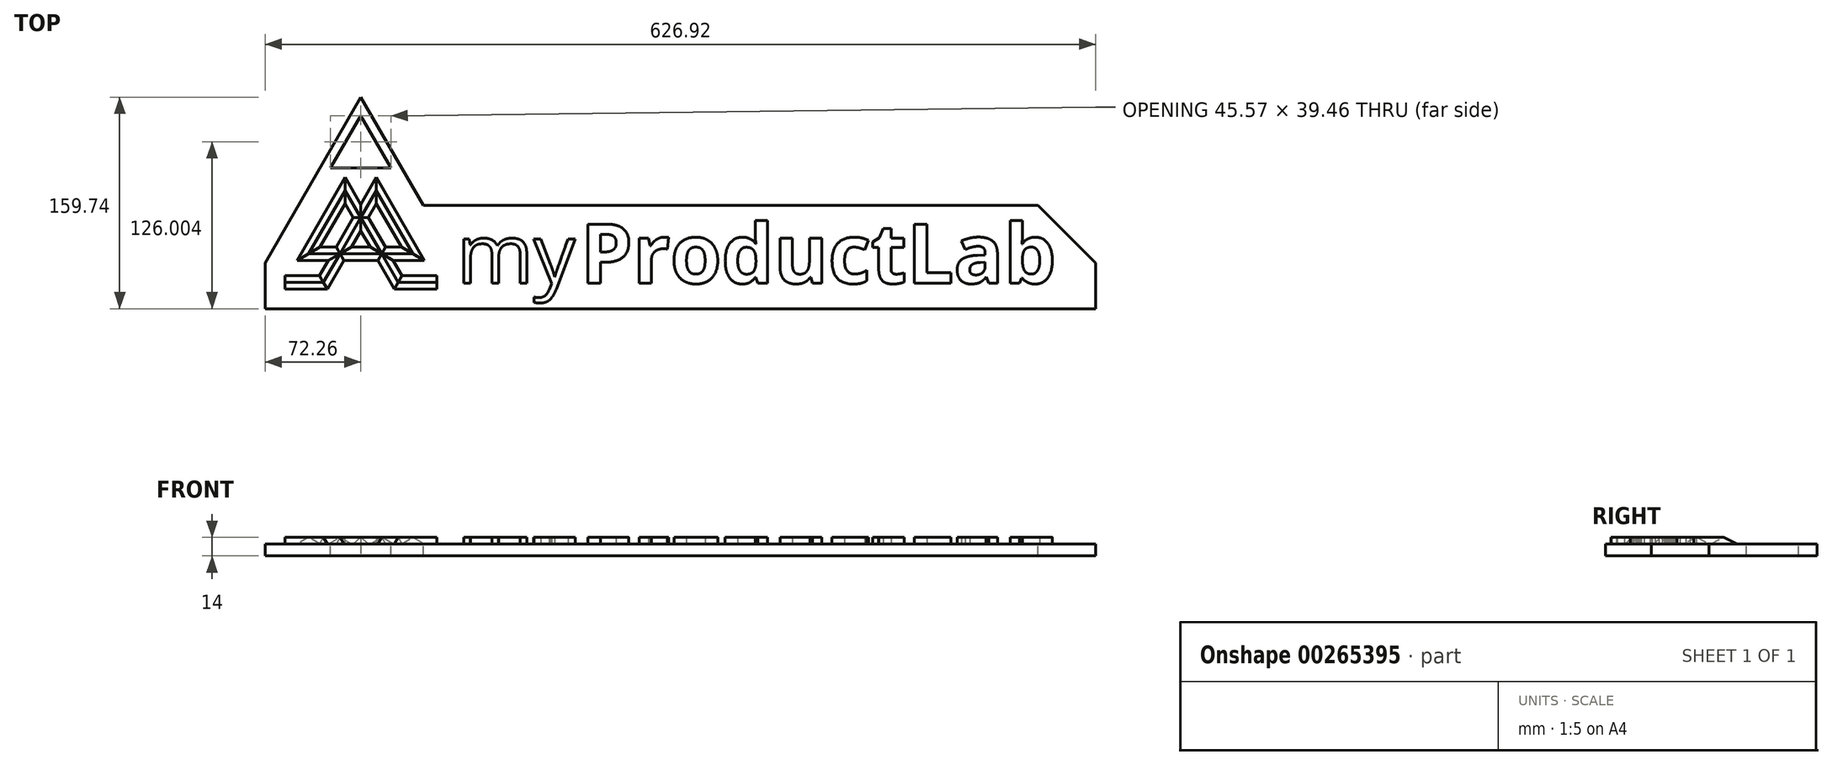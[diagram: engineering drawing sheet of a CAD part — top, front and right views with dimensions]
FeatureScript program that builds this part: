
annotation { "Feature Type Name" : "Feature", "Feature Type Description" : "" }
export const myFeature = defineFeature(function(context is Context, id is Id, definition is map)
    precondition{}
    {
        {
            var Q0;
            Q0=qCreatedBy(makeId("Top.planeOp"),FACE);
            var sketch = newSketch(context, id + "F0", { "sketchPlane" : qUnion([Q0])});
            skLineSegment(sketch, "E0", {"start": v(11.81, 20.46) * mm, "end": v(39.36, -27.25) * mm});
            skLineSegment(sketch, "E1", {"start": v(-39.36, -27.25) * mm, "end": v(-11.81, 20.46) * mm});
            skLineSegment(sketch, "E2", {"start": v(-11.81, 20.46) * mm, "end": v(28.18, -48.8) * mm});
            skLineSegment(sketch, "E3", {"start": v(28.18, -48.8) * mm, "end": v(57.26, -48.8) * mm});
            skLineSegment(sketch, "E4", {"start": v(-28.18, -48.8) * mm, "end": v(-57.26, -48.8) * mm});
            skLineSegment(sketch, "E5", {"start": v(-28.18, -48.8) * mm, "end": v(11.81, 20.46) * mm});
            skLineSegment(sketch, "E6", {"start": v(-39.36, -27.25) * mm, "end": v(0, -27.25) * mm});
            skLineSegment(sketch, "E7", {"start": v(0, -27.25) * mm, "end": v(39.36, -27.25) * mm});
            skSolve(sketch);
        }
        {
            var Q0;
            Q0=sQuery(id+"F0.wireOp",VERTEX,"E4.end");
            var Q1;
            Q1=sQuery(id+"F0.wireOp",EDGE,"E4");
            cPlane(context, id + "F1", {"entities" : qUnion([Q0, Q1]), "cplaneType" : CPlaneType.LINE_POINT, "offset" : 25 * mm, "width" : 150 * mm, "height" : 150 * mm});
        }
        {
            var Q0;
            Q0=qCreatedBy(id+"F1.planeOp",FACE);
            var sketch = newSketch(context, id + "F2", { "sketchPlane" : qUnion([Q0])});
            skLineSegment(sketch, "E8", {"start": v(48.8, 0) * mm, "end": v(43.8, -5) * mm});
            skLineSegment(sketch, "E9", {"start": v(43.8, -5) * mm, "end": v(53.8, -5) * mm});
            skLineSegment(sketch, "E10", {"start": v(53.8, -5) * mm, "end": v(48.8, 0) * mm});
            skSolve(sketch);
        }
        {
            var Q0;
            Q0=qSketchRegion(id+"F2",true);
            var Q1;
            Q1=sQuery(id+"F0.wireOp",EDGE,"E4");
            var Q2;
            Q2=sQuery(id+"F0.wireOp",EDGE,"E5");
            var Q3;
            Q3=sQuery(id+"F0.wireOp",EDGE,"E0");
            var Q4;
            Q4=sQuery(id+"F0.wireOp",EDGE,"E7");
            sweep(context, id + "F3", {"profiles" : qUnion([Q0]), "path" : qUnion([Q1, Q2, Q3, Q4])});
        }
        {
            var Q0;
            Q0=makeQuery(id+"F3.opSweep","SWEPT_BODY",BODY,{"disambiguationData":[OSD([sQuery(id+"F0.wireOp",EDGE,"E7"),sQuery(id+"F2.wireOp",EDGE,"E8"),sQuery(id+"F2.wireOp",EDGE,"E9"),sQuery(id+"F2.wireOp",EDGE,"E10")])]});
            var Q1;
            Q1=qCreatedBy(makeId("Right.planeOp"),FACE);
            mirror(context, id + "F4", {"operationType" : NewBodyOperationType.ADD, "entities" : qUnion([Q0]), "mirrorPlane" : qUnion([Q1])});
        }
        {
            var Q0;
            {var subQ0=makeQuery(id+"F3.opSweep","SWEPT_FACE",FACE,{"disambiguationData":[OSD([sQuery(id+"F0.wireOp",EDGE,"E4"),sQuery(id+"F2.wireOp",EDGE,"E9")])]});Q0=makeQuery(id+"F4.boolean.opBoolean","MERGE",FACE,{"derivedFrom":[subQ0,makeQuery(id+"F4.opPattern","COPY",FACE,{"derivedFrom":subQ0,"instanceName":"1"})]});}
            var sketch = newSketch(context, id + "F5", { "sketchPlane" : qUnion([Q0])});
            skLineSegment(sketch, "E11", {"start": v(-72.26, 68.8) * mm, "end": v(-72.26, -45.46) * mm});
            skLineSegment(sketch, "E12", {"start": v(-72.26, -45.46) * mm, "end": v(-8.93, -45.46) * mm});
            skLineSegment(sketch, "E13", {"start": v(8.93, -45.46) * mm, "end": v(557.26, -45.46) * mm});
            skLineSegment(sketch, "E14", {"start": v(557.26, 68.8) * mm, "end": v(-72.26, 68.8) * mm});
            skLineSegment(sketch, "E15", {"start": v(-32.02, -35.46) * mm, "end": v(-62.26, -35.46) * mm});
            skLineSegment(sketch, "E16", {"start": v(-62.26, -35.46) * mm, "end": v(-62.26, 16.92) * mm});
            skLineSegment(sketch, "E17", {"start": v(-62.26, 16.92) * mm, "end": v(-32.02, -35.46) * mm});
            skPoint(sketch, "E18.orphan", {"position": v(597.26, -45.46) * mm});
            skLineSegment(sketch, "E19", {"start": v(557.26, -45.46) * mm, "end": v(557.26, 68.8) * mm});
            skPoint(sketch, "E20.start.orphan", {"position": v(597.26, -15.46) * mm});
            skPoint(sketch, "E21.end.orphan", {"position": v(597.26, 38.8) * mm});
            skLineSegment(sketch, "E22", {"start": v(-8.93, -45.46) * mm, "end": v(8.93, -45.46) * mm});
            skPoint(sketch, "E23.end.orphan", {"position": v(0, -35) * mm});
            skSolve(sketch);
        }
        {
            var Q0;
            Q0 = qSketchRegion(id + "F5", true);
            extrude(context, id + "F6", {"entities" : qUnion([Q0]), "operationType" : NewBodyOperationType.ADD, "depth" : 5 * mm});
        }
        {
            var Q0;
            {var subQ0=sQuery(id+"F5.wireOp",EDGE,"E14");var subQ1=sQuery(id+"F5.wireOp",EDGE,"E13");var subQ2=sQuery(id+"F5.wireOp",EDGE,"E11");var subQ3=sQuery(id+"F5.wireOp",EDGE,"E23");var subQ4=sQuery(id+"F5.wireOp",EDGE,"E12");var subQ5=sQuery(id+"F5.wireOp",EDGE,"E20");var subQ6=sQuery(id+"F2.wireOp",EDGE,"E8");var subQ7=makeQuery(id+"F3.opSweep","SWEPT_FACE",FACE,{"disambiguationData":[OSD([sQuery(id+"F0.wireOp",EDGE,"E7"),subQ6])]});var subQ8=sQuery(id+"F5.wireOp",EDGE,"E15");var subQ9=sQuery(id+"F2.wireOp",EDGE,"E10");var subQ10=sQuery(id+"F0.wireOp",EDGE,"E4");var subQ11=makeQuery(id+"F3.opSweep","SWEPT_FACE",FACE,{"disambiguationData":[OSD([subQ10,subQ9])]});var subQ12=sQuery(id+"F0.wireOp",EDGE,"E5");var subQ13=makeQuery(id+"F3.opSweep","SWEPT_FACE",FACE,{"disambiguationData":[OSD([subQ12,subQ9])]});var subQ14=makeQuery(id+"F3.opSweep","SWEPT_FACE",FACE,{"disambiguationData":[OSD([subQ10,subQ6])]});var subQ15=makeQuery(id+"F3.opSweep","SWEPT_FACE",FACE,{"disambiguationData":[OSD([sQuery(id+"F0.wireOp",EDGE,"E0"),subQ6])]});var subQ16=makeQuery(id+"F3.opSweep","CAP_FACE",FACE,{"disambiguationData":[OSD([sQuery(id+"F0.wireOp",VERTEX,"E4.end"),subQ6,sQuery(id+"F2.wireOp",EDGE,"E9"),subQ9])],"isStart":true});var subQ17=makeQuery(id+"F3.opSweep","SWEPT_FACE",FACE,{"disambiguationData":[OSD([subQ12,subQ6])]});var subQ18=sQuery(id+"F5.wireOp",EDGE,"J89TbGMw-nEVW-EWQc-egT6-3zY5aMVhYpZx");var subQ19=sQuery(id+"F5.wireOp",EDGE,"E16");var subQ20=sQuery(id+"F5.wireOp",EDGE,"E17");Q0=makeQuery(id+"F6.boolean.opBoolean","SPLIT",FACE,{"disambiguationData":[TD([subQ16,subQ15,subQ14,subQ11,subQ17,subQ13,subQ7,makeQuery(id+"F4.opPattern","COPY",FACE,{"derivedFrom":subQ16,"instanceName":"1"}),makeQuery(id+"F4.opPattern","COPY",FACE,{"derivedFrom":subQ15,"instanceName":"1"}),makeQuery(id+"F4.opPattern","COPY",FACE,{"derivedFrom":subQ14,"instanceName":"1"}),makeQuery(id+"F4.opPattern","COPY",FACE,{"derivedFrom":subQ11,"instanceName":"1"}),makeQuery(id+"F4.opPattern","COPY",FACE,{"derivedFrom":subQ17,"instanceName":"1"}),makeQuery(id+"F4.opPattern","COPY",FACE,{"derivedFrom":subQ13,"instanceName":"1"}),makeQuery(id+"F4.opPattern","COPY",FACE,{"derivedFrom":subQ7,"instanceName":"1"}),makeQuery(id+"F6.opExtrude","SWEPT_FACE",FACE,{"disambiguationData":[OSD([subQ2])]}),makeQuery(id+"F6.opExtrude","SWEPT_FACE",FACE,{"disambiguationData":[OSD([subQ4])]}),makeQuery(id+"F6.opExtrude","SWEPT_FACE",FACE,{"disambiguationData":[OSD([subQ3])]}),makeQuery(id+"F6.opExtrude","SWEPT_FACE",FACE,{"disambiguationData":[OSD([subQ18])]}),makeQuery(id+"F6.opExtrude","SWEPT_FACE",FACE,{"disambiguationData":[OSD([subQ1])]}),makeQuery(id+"F6.opExtrude","SWEPT_FACE",FACE,{"disambiguationData":[OSD([subQ5])]}),makeQuery(id+"F6.opExtrude","SWEPT_FACE",FACE,{"disambiguationData":[OSD([subQ0])]}),makeQuery(id+"F6.opExtrude","SWEPT_FACE",FACE,{"disambiguationData":[OSD([subQ8])]}),makeQuery(id+"F6.opExtrude","SWEPT_FACE",FACE,{"disambiguationData":[OSD([subQ19])]}),makeQuery(id+"F6.opExtrude","SWEPT_FACE",FACE,{"disambiguationData":[OSD([subQ20])]})])],"derivedFrom":makeQuery(id+"F6.opExtrude","CAP_FACE",FACE,{"disambiguationData":[OSD([subQ2,subQ4,subQ3,subQ18,subQ1,subQ5,subQ0,subQ8,subQ19,subQ20])],"isStart":true})});}
            var sketch = newSketch(context, id + "F7", { "sketchPlane" : qUnion([Q0])});
            skText(sketch, "E24", { "text": "my", "fontName": "OpenSans-Regular.ttf"});
            skText(sketch, "E25", { "text": "ProductLab", "fontName": "OpenSans-Bold.ttf"});
            const initialGuessF7  = {"E24": [0.07226, -0.04954, 1, 0, 0.045], "E25": [0.16589, -0.04954, 1, 0, 0.045]};
            skSetInitialGuess(sketch, initialGuessF7);
            skSolve(sketch);
        }
        {
            var Q0;
            Q0 = qSketchRegion(id + "F7", true);
            extrude(context, id + "F8", {"entities" : qUnion([Q0]), "operationType" : NewBodyOperationType.ADD, "depth" : 5 * mm});
        }
        {
            var Q0;
            {var subQ0=sQuery(id+"F5.wireOp",EDGE,"J89TbGMw-nEVW-EWQc-egT6-3zY5aMVhYpZx");var subQ1=makeQuery(id+"F6.opExtrude","SWEPT_FACE",FACE,{"disambiguationData":[OSD([subQ0])]});var subQ2=sQuery(id+"F5.wireOp",EDGE,"E20");var subQ3=makeQuery(id+"F6.opExtrude","SWEPT_FACE",FACE,{"disambiguationData":[OSD([subQ2])]});var subQ4=sQuery(id+"F5.wireOp",EDGE,"Xyr0NvYb-IOld-dSm6-9Bcy-tAYvncZcYHa3");var subQ5=makeQuery(id+"F6.opExtrude","SWEPT_FACE",FACE,{"disambiguationData":[OSD([subQ4])]});var subQ6=sQuery(id+"F2.wireOp",EDGE,"E8");var subQ7=makeQuery(id+"F3.opSweep","SWEPT_FACE",FACE,{"disambiguationData":[OSD([sQuery(id+"F0.wireOp",EDGE,"E7"),subQ6])]});var subQ8=makeQuery(id+"F4.opPattern","COPY",FACE,{"derivedFrom":subQ7,"instanceName":"1"});var subQ9=sQuery(id+"F0.wireOp",EDGE,"E4");var subQ10=makeQuery(id+"F3.opSweep","SWEPT_FACE",FACE,{"disambiguationData":[OSD([subQ9,subQ6])]});var subQ11=sQuery(id+"F5.wireOp",EDGE,"E21");var subQ12=makeQuery(id+"F6.opExtrude","SWEPT_FACE",FACE,{"disambiguationData":[OSD([subQ11])]});var subQ13=makeQuery(id+"F3.opSweep","SWEPT_FACE",FACE,{"disambiguationData":[OSD([sQuery(id+"F0.wireOp",EDGE,"E0"),subQ6])]});var subQ14=makeQuery(id+"F4.opPattern","COPY",FACE,{"derivedFrom":subQ13,"instanceName":"1"});var subQ15=makeQuery(id+"F4.opPattern","COPY",FACE,{"derivedFrom":subQ10,"instanceName":"1"});var subQ16=sQuery(id+"F5.wireOp",EDGE,"E15");var subQ17=makeQuery(id+"F6.opExtrude","SWEPT_FACE",FACE,{"disambiguationData":[OSD([subQ16])]});var subQ18=sQuery(id+"F0.wireOp",EDGE,"E5");var subQ19=makeQuery(id+"F3.opSweep","SWEPT_FACE",FACE,{"disambiguationData":[OSD([subQ18,subQ6])]});var subQ20=makeQuery(id+"F4.opPattern","COPY",FACE,{"derivedFrom":subQ19,"instanceName":"1"});var subQ21=sQuery(id+"F2.wireOp",EDGE,"E10");var subQ22=makeQuery(id+"F3.opSweep","CAP_FACE",FACE,{"disambiguationData":[OSD([sQuery(id+"F0.wireOp",VERTEX,"E4.end"),subQ6,sQuery(id+"F2.wireOp",EDGE,"E9"),subQ21])],"isStart":true});var subQ23=makeQuery(id+"F3.opSweep","SWEPT_FACE",FACE,{"disambiguationData":[OSD([subQ18,subQ21])]});var subQ24=makeQuery(id+"F3.opSweep","SWEPT_FACE",FACE,{"disambiguationData":[OSD([subQ9,subQ21])]});var subQ25=sQuery(id+"F5.wireOp",EDGE,"E17");var subQ26=makeQuery(id+"F6.opExtrude","SWEPT_FACE",FACE,{"disambiguationData":[OSD([subQ25])]});var subQ27=makeQuery(id+"F4.opPattern","COPY",FACE,{"derivedFrom":subQ23,"instanceName":"1"});var subQ28=sQuery(id+"F5.wireOp",EDGE,"E13");var subQ29=makeQuery(id+"F6.opExtrude","SWEPT_FACE",FACE,{"disambiguationData":[OSD([subQ28])]});var subQ30=makeQuery(id+"F4.opPattern","COPY",FACE,{"derivedFrom":subQ24,"instanceName":"1"});var subQ31=sQuery(id+"F5.wireOp",EDGE,"E11");var subQ32=makeQuery(id+"F6.opExtrude","SWEPT_FACE",FACE,{"disambiguationData":[OSD([subQ31])]});var subQ33=sQuery(id+"F5.wireOp",EDGE,"E23");var subQ34=makeQuery(id+"F6.opExtrude","SWEPT_FACE",FACE,{"disambiguationData":[OSD([subQ33])]});var subQ35=makeQuery(id+"F4.opPattern","COPY",FACE,{"derivedFrom":subQ22,"instanceName":"1"});var subQ36=sQuery(id+"F5.wireOp",EDGE,"E12");var subQ37=makeQuery(id+"F6.opExtrude","SWEPT_FACE",FACE,{"disambiguationData":[OSD([subQ36])]});var subQ38=sQuery(id+"F5.wireOp",EDGE,"E14");var subQ39=makeQuery(id+"F6.opExtrude","SWEPT_FACE",FACE,{"disambiguationData":[OSD([subQ38])]});var subQ40=sQuery(id+"F5.wireOp",EDGE,"E16");var subQ41=makeQuery(id+"F6.opExtrude","SWEPT_FACE",FACE,{"disambiguationData":[OSD([subQ40])]});Q0=makeQuery(id+"F8.boolean.opBoolean","SPLIT",FACE,{"disambiguationData":[TD([subQ32])],"derivedFrom":makeQuery(id+"F6.boolean.opBoolean","SPLIT",FACE,{"disambiguationData":[TD([subQ22,subQ13,subQ10,subQ24,subQ19,subQ23,subQ7,subQ35,subQ14,subQ15,subQ30,subQ20,subQ27,subQ8,subQ32,subQ37,subQ34,subQ1,subQ29,subQ3,subQ39,subQ17,subQ41,subQ26,subQ5,subQ12])],"derivedFrom":makeQuery(id+"F6.opExtrude","CAP_FACE",FACE,{"disambiguationData":[OSD([subQ31,subQ36,subQ33,subQ0,subQ28,subQ2,subQ38,subQ16,subQ40,subQ25,subQ4,subQ11])],"isStart":true})})});}
            var sketch = newSketch(context, id + "F9", { "sketchPlane" : qUnion([Q0])});
            skPoint(sketch, "E26.endSnap0", {"position": v(220.32, -15.58) * mm});
            skLineSegment(sketch, "E27", {"start": v(557.26, -11.67) * mm, "end": v(-293.74, -11.67) * mm, "construction": true});
            skPoint(sketch, "E27.endSnap0", {"position": v(-72.26, -11.67) * mm});
            skLineSegment(sketch, "E28", {"start": v(557.26, 9.24) * mm, "end": v(557.26, 45.46) * mm});
            skLineSegment(sketch, "E29", {"start": v(557.26, 45.46) * mm, "end": v(26.25, 45.46) * mm});
            skLineSegment(sketch, "E30", {"start": v(26.25, 45.46) * mm, "end": v(47.16, 9.24) * mm});
            skLineSegment(sketch, "E31", {"start": v(47.16, 9.24) * mm, "end": v(557.26, 9.24) * mm});
            skSolve(sketch);
        }
        {
            var Q0;
            Q0 = qSketchRegion(id + "F9", true);
            extrude(context, id + "F10", {"entities" : qUnion([Q0]), "operationType" : NewBodyOperationType.REMOVE, "oppositeDirection" : true, "depth" : 25 * mm});
        }
        {
            var Q0;
            Q0=makeQuery(id+"F10.boolean.opBoolean","COPY",EDGE,{"derivedFrom":makeQuery(id+"F10.opExtrude","SWEPT_EDGE",EDGE,{"disambiguationData":[OSD([sQuery(id+"F5.wireOp",EDGE,"E19"),sQuery(id+"F9.wireOp",EDGE,"3NKoLEs0-C7rr-6Oif-dHGT-x0XMBWaBHwz6"),sQuery(id+"F9.wireOp",EDGE,"E28")])]})});
            var Q1;
            Q1=makeQuery(id+"F6.opExtrude","SWEPT_EDGE",EDGE,{"disambiguationData":[OSD([sQuery(id+"F5.wireOp",EDGE,"E14"),sQuery(id+"F5.wireOp",EDGE,"E19")])]});
            chamfer(context, id + "F11", {"entities" : qUnion([Q0, Q1]), "width" : 25 * mm, "tangentPropagation" : true});
        }
        {
            var Q0;
            {var subQ0=sQuery(id+"F5.wireOp",EDGE,"E17");var subQ1=makeQuery(id+"F6.opExtrude","SWEPT_FACE",FACE,{"disambiguationData":[OSD([subQ0])]});var subQ2=sQuery(id+"F5.wireOp",EDGE,"E19");var subQ3=makeQuery(id+"F6.opExtrude","SWEPT_FACE",FACE,{"disambiguationData":[OSD([subQ2])]});var subQ4=sQuery(id+"F5.wireOp",EDGE,"E22");var subQ5=sQuery(id+"F5.wireOp",EDGE,"E13");var subQ6=sQuery(id+"F5.wireOp",EDGE,"E12");var subQ7=makeQuery(id+"F6.opExtrude","SWEPT_FACE",FACE,{"disambiguationData":[OSD([subQ6,subQ5,subQ4])]});var subQ8=sQuery(id+"F2.wireOp",EDGE,"E10");var subQ9=sQuery(id+"F2.wireOp",EDGE,"E8");var subQ10=makeQuery(id+"F3.opSweep","CAP_FACE",FACE,{"disambiguationData":[OSD([sQuery(id+"F0.wireOp",VERTEX,"E4.end"),subQ9,sQuery(id+"F2.wireOp",EDGE,"E9"),subQ8])],"isStart":true});var subQ11=makeQuery(id+"F4.opPattern","COPY",FACE,{"derivedFrom":subQ10,"instanceName":"1"});var subQ12=sQuery(id+"F5.wireOp",EDGE,"E14");var subQ13=makeQuery(id+"F6.opExtrude","SWEPT_FACE",FACE,{"disambiguationData":[OSD([subQ12])]});var subQ14=sQuery(id+"F5.wireOp",EDGE,"E15");var subQ15=makeQuery(id+"F6.opExtrude","SWEPT_FACE",FACE,{"disambiguationData":[OSD([subQ14])]});var subQ16=sQuery(id+"F0.wireOp",EDGE,"E4");var subQ17=makeQuery(id+"F3.opSweep","SWEPT_FACE",FACE,{"disambiguationData":[OSD([subQ16,subQ8])]});var subQ18=makeQuery(id+"F4.opPattern","COPY",FACE,{"derivedFrom":subQ17,"instanceName":"1"});var subQ19=sQuery(id+"F5.wireOp",EDGE,"E16");var subQ20=makeQuery(id+"F6.opExtrude","SWEPT_FACE",FACE,{"disambiguationData":[OSD([subQ19])]});var subQ21=sQuery(id+"F0.wireOp",EDGE,"E5");var subQ22=makeQuery(id+"F3.opSweep","SWEPT_FACE",FACE,{"disambiguationData":[OSD([subQ21,subQ8])]});var subQ23=makeQuery(id+"F4.opPattern","COPY",FACE,{"derivedFrom":subQ22,"instanceName":"1"});var subQ24=makeQuery(id+"F3.opSweep","SWEPT_FACE",FACE,{"disambiguationData":[OSD([subQ16,subQ9])]});var subQ25=makeQuery(id+"F3.opSweep","SWEPT_FACE",FACE,{"disambiguationData":[OSD([sQuery(id+"F0.wireOp",EDGE,"E0"),subQ9])]});var subQ26=makeQuery(id+"F3.opSweep","SWEPT_FACE",FACE,{"disambiguationData":[OSD([subQ21,subQ9])]});var subQ27=makeQuery(id+"F4.opPattern","COPY",FACE,{"derivedFrom":subQ26,"instanceName":"1"});var subQ28=makeQuery(id+"F3.opSweep","SWEPT_FACE",FACE,{"disambiguationData":[OSD([sQuery(id+"F0.wireOp",EDGE,"E7"),subQ9])]});var subQ29=makeQuery(id+"F4.opPattern","COPY",FACE,{"derivedFrom":subQ24,"instanceName":"1"});var subQ30=makeQuery(id+"F4.opPattern","COPY",FACE,{"derivedFrom":subQ25,"instanceName":"1"});var subQ31=makeQuery(id+"F4.opPattern","COPY",FACE,{"derivedFrom":subQ28,"instanceName":"1"});var subQ32=sQuery(id+"F5.wireOp",EDGE,"E11");var subQ33=makeQuery(id+"F6.opExtrude","SWEPT_FACE",FACE,{"disambiguationData":[OSD([subQ32])]});Q0=makeQuery(id+"F8.boolean.opBoolean","SPLIT",FACE,{"disambiguationData":[TD([subQ33])],"derivedFrom":makeQuery(id+"F6.boolean.opBoolean","SPLIT",FACE,{"disambiguationData":[TD([subQ10,subQ25,subQ24,subQ17,subQ26,subQ22,subQ28,subQ11,subQ30,subQ29,subQ18,subQ27,subQ23,subQ31,subQ33,subQ7,subQ13,subQ15,subQ20,subQ1,subQ3])],"derivedFrom":makeQuery(id+"F6.opExtrude","CAP_FACE",FACE,{"disambiguationData":[OSD([subQ32,subQ6,subQ5,subQ12,subQ14,subQ19,subQ0,subQ2,subQ4])],"isStart":true})})});}
            var sketch = newSketch(context, id + "F12", { "sketchPlane" : qUnion([Q0])});
            skLineSegment(sketch, "E32.0", {"start": v(-72.26, 45.46) * mm, "end": v(26.25, 45.46) * mm});
            skPoint(sketch, "E33.0", {"position": v(36.7, 27.35) * mm});
            skLineSegment(sketch, "E34.0", {"start": v(26.25, 45.46) * mm, "end": v(47.16, 9.24) * mm});
            skLineSegment(sketch, "E35.0", {"start": v(47.16, 9.24) * mm, "end": v(532.26, 9.24) * mm});
            skPoint(sketch, "E36.0", {"position": v(544.76, -3.26) * mm});
            skPoint(sketch, "E37.0", {"position": v(557.26, -29.78) * mm});
            skLineSegment(sketch, "E38.0", {"start": v(557.26, -15.76) * mm, "end": v(557.26, -43.8) * mm});
            skLineSegment(sketch, "E39.0", {"start": v(557.26, -15.76) * mm, "end": v(532.26, 9.24) * mm});
            skLineSegment(sketch, "E40.0", {"start": v(532.26, -68.8) * mm, "end": v(557.26, -43.8) * mm});
            skLineSegment(sketch, "E41.0", {"start": v(532.26, -68.8) * mm, "end": v(-72.26, -68.8) * mm});
            skLineSegment(sketch, "E42.0", {"start": v(-72.26, -68.8) * mm, "end": v(-72.26, 45.46) * mm});
            skLineSegment(sketch, "E43.0", {"start": v(22.78, 39.46) * mm, "end": v(43.7, 3.24) * mm});
            skLineSegment(sketch, "E43.1", {"start": v(-66.26, 39.46) * mm, "end": v(22.78, 39.46) * mm});
            skLineSegment(sketch, "E43.2", {"start": v(43.7, 3.24) * mm, "end": v(529.78, 3.24) * mm});
            skLineSegment(sketch, "E43.3", {"start": v(-66.26, -62.8) * mm, "end": v(-66.26, 39.46) * mm});
            skLineSegment(sketch, "E43.4", {"start": v(551.26, -18.25) * mm, "end": v(529.78, 3.24) * mm});
            skLineSegment(sketch, "E43.5", {"start": v(551.26, -18.25) * mm, "end": v(551.26, -41.32) * mm});
            skLineSegment(sketch, "E43.6", {"start": v(529.78, -62.8) * mm, "end": v(551.26, -41.32) * mm});
            skLineSegment(sketch, "E43.7", {"start": v(529.78, -62.8) * mm, "end": v(-66.26, -62.8) * mm});
            skSolve(sketch);
        }
        {
            var Q0;
            Q0=makeQuery(id+"F12.imprint","IMPRINT",FACE,{"disambiguationData":[TD([[makeQuery(id+"F12.imprint","IMPRINT",EDGE,{"derivedFrom":sQuery(id+"F12.wireOp",EDGE,"E43.0")}),-1.0]])]});
            var sketch = newSketch(context, id + "F13", { "sketchPlane" : qUnion([Q0])});
            skLineSegment(sketch, "E44", {"start": v(26.25, 45.46) * mm, "end": v(532.26, 9.24) * mm});
            skLineSegment(sketch, "E45", {"start": v(532.26, 9.24) * mm, "end": v(462.24, 9.24) * mm});
            skLineSegment(sketch, "E46", {"start": v(462.24, 9.24) * mm, "end": v(29.27, 40.23) * mm});
            skLineSegment(sketch, "E47", {"start": v(29.27, 40.23) * mm, "end": v(26.25, 45.46) * mm});
            skSolve(sketch);
        }
        {
            var Q0;
            Q0 = qSketchRegion(id + "F13", true);
            extrude(context, id + "F14", {"entities" : qUnion([Q0]), "operationType" : NewBodyOperationType.ADD, "oppositeDirection" : true, "depth" : 5 * mm});
        }
        {
            var Q0;
            Q0=makeQuery(id+"F12.imprint","IMPRINT",FACE,{"disambiguationData":[TD([[makeQuery(id+"F12.imprint","IMPRINT",EDGE,{"derivedFrom":sQuery(id+"F12.wireOp",EDGE,"E43.0")}),-1.0]])]});
            var sketch = newSketch(context, id + "F15", { "sketchPlane" : qUnion([Q0])});
            skSolve(sketch);
        }
        {
            var Q0;
            Q0=makeQuery(id+"F14.boolean.opBoolean","MERGE",FACE,{"derivedFrom":[makeQuery(id+"F6.opExtrude","CAP_FACE",FACE,{"disambiguationData":[OSD([sQuery(id+"F5.wireOp",EDGE,"E11"),sQuery(id+"F5.wireOp",EDGE,"E12"),sQuery(id+"F5.wireOp",EDGE,"E13"),sQuery(id+"F5.wireOp",EDGE,"E14"),sQuery(id+"F5.wireOp",EDGE,"E15"),sQuery(id+"F5.wireOp",EDGE,"E16"),sQuery(id+"F5.wireOp",EDGE,"E17"),sQuery(id+"F5.wireOp",EDGE,"E19"),sQuery(id+"F5.wireOp",EDGE,"E22")])],"isStart":false}),makeQuery(id+"F14.opExtrude","CAP_FACE",FACE,{"disambiguationData":[OSD([sQuery(id+"F13.wireOp",EDGE,"E44"),sQuery(id+"F13.wireOp",EDGE,"E45"),sQuery(id+"F13.wireOp",EDGE,"E46"),sQuery(id+"F13.wireOp",EDGE,"E47")])],"isStart":false})]});
            var sketch = newSketch(context, id + "F16", { "sketchPlane" : qUnion([Q0])});
            skLineSegment(sketch, "E48", {"start": v(-72.26, -45.46) * mm, "end": v(-72.26, -50.46) * mm});
            skLineSegment(sketch, "E49.0", {"start": v(534.33, 73.8) * mm, "end": v(-72.26, 73.8) * mm});
            skLineSegment(sketch, "E49.1", {"start": v(534.33, 73.8) * mm, "end": v(562.26, 45.88) * mm});
            skLineSegment(sketch, "E49.2", {"start": v(-72.26, -50.46) * mm, "end": v(26.43, -50.46) * mm});
            skLineSegment(sketch, "E49.3", {"start": v(26.43, -50.46) * mm, "end": v(534.48, -14.1) * mm});
            skLineSegment(sketch, "E49.4", {"start": v(562.26, 13.69) * mm, "end": v(534.48, -14.1) * mm});
            skLineSegment(sketch, "E49.5", {"start": v(562.26, 13.69) * mm, "end": v(562.26, 45.88) * mm});
            skLineSegment(sketch, "E50", {"start": v(-72.26, 73.8) * mm, "end": v(-72.26, 68.8) * mm});
            skLineSegment(sketch, "E51.0", {"start": v(-72.26, -45.46) * mm, "end": v(26.25, -45.46) * mm});
            skLineSegment(sketch, "E52.0", {"start": v(26.25, -45.46) * mm, "end": v(532.26, -9.24) * mm});
            skLineSegment(sketch, "E53.0", {"start": v(557.26, 15.76) * mm, "end": v(532.26, -9.24) * mm});
            skLineSegment(sketch, "E54.0", {"start": v(557.26, 15.76) * mm, "end": v(557.26, 43.8) * mm});
            skLineSegment(sketch, "E55.0", {"start": v(532.26, 68.8) * mm, "end": v(557.26, 43.8) * mm});
            skLineSegment(sketch, "E56.0", {"start": v(532.26, 68.8) * mm, "end": v(-72.26, 68.8) * mm});
            skSolve(sketch);
        }
        {
            var Q0;
            Q0 = qSketchRegion(id + "F16", true);
            extrude(context, id + "F17", {"entities" : qUnion([Q0]), "operationType" : NewBodyOperationType.ADD, "oppositeDirection" : true, "depth" : 5 * mm});
        }
        {
            var Q0;
            Q0=makeQuery(id+"F15.imprint","IMPRINT",FACE,{"disambiguationData":[TD([[makeQuery(id+"F15.imprint","IMPRINT",EDGE,{"derivedFrom":makeQuery(id+"F12.imprint","IMPRINT",EDGE,{"derivedFrom":sQuery(id+"F12.wireOp",EDGE,"E43.0")})}),-1.0]])]});
            var sketch = newSketch(context, id + "F18", { "sketchPlane" : qUnion([Q0])});
            skLineSegment(sketch, "E57", {"start": v(-95.15, -73.88) * mm, "end": v(-7.88, 77.28) * mm});
            skLineSegment(sketch, "E58", {"start": v(-7.88, 77.28) * mm, "end": v(-102.86, 77.28) * mm});
            skLineSegment(sketch, "E59", {"start": v(-102.86, 77.28) * mm, "end": v(-95.15, -73.88) * mm});
            skSolve(sketch);
        }
        {
            var Q0;
            Q0 = qSketchRegion(id + "F18", true);
            extrude(context, id + "F19", {"entities" : qUnion([Q0]), "operationType" : NewBodyOperationType.REMOVE, "oppositeDirection" : true, "depth" : 25 * mm});
        }
        {
            var Q0;
            Q0=makeQuery(id+"F15.imprint","IMPRINT",FACE,{"disambiguationData":[TD([[makeQuery(id+"F15.imprint","IMPRINT",EDGE,{"derivedFrom":makeQuery(id+"F12.imprint","IMPRINT",EDGE,{"derivedFrom":sQuery(id+"F12.wireOp",EDGE,"E43.0")})}),-1.0]])]});
            var sketch = newSketch(context, id + "F20", { "sketchPlane" : qUnion([Q0])});
            skLineSegment(sketch, "E60", {"start": v(534.48, 16.87) * mm, "end": v(534.48, -68.8) * mm});
            skLineSegment(sketch, "E61", {"start": v(534.48, -79.9) * mm, "end": v(584.33, -78.57) * mm});
            skLineSegment(sketch, "E62", {"start": v(584.33, -78.57) * mm, "end": v(562.44, 10.18) * mm});
            skLineSegment(sketch, "E63", {"start": v(562.44, 10.18) * mm, "end": v(534.48, 16.87) * mm});
            skLineSegment(sketch, "E64", {"start": v(534.48, -68.8) * mm, "end": v(-141.37, -68.8) * mm});
            skLineSegment(sketch, "E65", {"start": v(-141.37, -68.8) * mm, "end": v(-141.37, -83.35) * mm});
            skLineSegment(sketch, "E66", {"start": v(-141.37, -83.35) * mm, "end": v(534.48, -79.9) * mm});
            skSolve(sketch);
        }
        {
            var Q0;
            Q0 = qSketchRegion(id + "F20", true);
            extrude(context, id + "F21", {"entities" : qUnion([Q0]), "operationType" : NewBodyOperationType.REMOVE, "oppositeDirection" : true, "depth" : 25 * mm});
        }
        {
            var Q0;
            Q0=makeQuery(id+"F17.boolean.opBoolean","MERGE",FACE,{"derivedFrom":[makeQuery(id+"F14.boolean.opBoolean","MERGE",FACE,{"derivedFrom":[makeQuery(id+"F6.opExtrude","CAP_FACE",FACE,{"disambiguationData":[OSD([sQuery(id+"F5.wireOp",EDGE,"E11"),sQuery(id+"F5.wireOp",EDGE,"E12"),sQuery(id+"F5.wireOp",EDGE,"E13"),sQuery(id+"F5.wireOp",EDGE,"E14"),sQuery(id+"F5.wireOp",EDGE,"E15"),sQuery(id+"F5.wireOp",EDGE,"E16"),sQuery(id+"F5.wireOp",EDGE,"E17"),sQuery(id+"F5.wireOp",EDGE,"E19"),sQuery(id+"F5.wireOp",EDGE,"E22")])],"isStart":false}),makeQuery(id+"F14.opExtrude","CAP_FACE",FACE,{"disambiguationData":[OSD([sQuery(id+"F13.wireOp",EDGE,"E44"),sQuery(id+"F13.wireOp",EDGE,"E45"),sQuery(id+"F13.wireOp",EDGE,"E46"),sQuery(id+"F13.wireOp",EDGE,"E47")])],"isStart":false})]}),makeQuery(id+"F17.opExtrude","CAP_FACE",FACE,{"disambiguationData":[OSD([sQuery(id+"F16.wireOp",EDGE,"E48"),sQuery(id+"F16.wireOp",EDGE,"E49.0"),sQuery(id+"F16.wireOp",EDGE,"E49.1"),sQuery(id+"F16.wireOp",EDGE,"E49.2"),sQuery(id+"F16.wireOp",EDGE,"E49.3"),sQuery(id+"F16.wireOp",EDGE,"E49.4"),sQuery(id+"F16.wireOp",EDGE,"E49.5"),sQuery(id+"F16.wireOp",EDGE,"E50"),sQuery(id+"F16.wireOp",EDGE,"E51.0"),sQuery(id+"F16.wireOp",EDGE,"E52.0"),sQuery(id+"F16.wireOp",EDGE,"E53.0"),sQuery(id+"F16.wireOp",EDGE,"E54.0"),sQuery(id+"F16.wireOp",EDGE,"E55.0"),sQuery(id+"F16.wireOp",EDGE,"E56.0")])],"isStart":true})]});
            var sketch = newSketch(context, id + "F22", { "sketchPlane" : qUnion([Q0])});
            skLineSegment(sketch, "E67", {"start": v(534.48, -14.1) * mm, "end": v(534.48, 68.8) * mm});
            skLineSegment(sketch, "E68", {"start": v(534.48, 68.8) * mm, "end": v(581.31, 68.8) * mm});
            skLineSegment(sketch, "E69", {"start": v(581.31, 34.24) * mm, "end": v(534.48, -14.1) * mm});
            skLineSegment(sketch, "E70", {"start": v(581.31, 34.24) * mm, "end": v(581.31, 68.8) * mm});
            skSolve(sketch);
        }
        {
            var Q0;
            Q0 = qSketchRegion(id + "F22", true);
            extrude(context, id + "F23", {"entities" : qUnion([Q0]), "operationType" : NewBodyOperationType.ADD, "oppositeDirection" : true, "depth" : 5 * mm});
        }
        {
            var Q0;
            Q0=makeQuery(id+"F23.boolean.opBoolean","MERGE",FACE,{"derivedFrom":[makeQuery(id+"F17.boolean.opBoolean","MERGE",FACE,{"derivedFrom":[makeQuery(id+"F14.boolean.opBoolean","MERGE",FACE,{"derivedFrom":[makeQuery(id+"F6.opExtrude","CAP_FACE",FACE,{"disambiguationData":[OSD([sQuery(id+"F5.wireOp",EDGE,"E11"),sQuery(id+"F5.wireOp",EDGE,"E12"),sQuery(id+"F5.wireOp",EDGE,"E13"),sQuery(id+"F5.wireOp",EDGE,"E14"),sQuery(id+"F5.wireOp",EDGE,"E15"),sQuery(id+"F5.wireOp",EDGE,"E16"),sQuery(id+"F5.wireOp",EDGE,"E17"),sQuery(id+"F5.wireOp",EDGE,"E19"),sQuery(id+"F5.wireOp",EDGE,"E22")])],"isStart":false}),makeQuery(id+"F14.opExtrude","CAP_FACE",FACE,{"disambiguationData":[OSD([sQuery(id+"F13.wireOp",EDGE,"E44"),sQuery(id+"F13.wireOp",EDGE,"E45"),sQuery(id+"F13.wireOp",EDGE,"E46"),sQuery(id+"F13.wireOp",EDGE,"E47")])],"isStart":false})]}),makeQuery(id+"F17.opExtrude","CAP_FACE",FACE,{"disambiguationData":[OSD([sQuery(id+"F16.wireOp",EDGE,"E48"),sQuery(id+"F16.wireOp",EDGE,"E49.0"),sQuery(id+"F16.wireOp",EDGE,"E49.1"),sQuery(id+"F16.wireOp",EDGE,"E49.2"),sQuery(id+"F16.wireOp",EDGE,"E49.3"),sQuery(id+"F16.wireOp",EDGE,"E49.4"),sQuery(id+"F16.wireOp",EDGE,"E49.5"),sQuery(id+"F16.wireOp",EDGE,"E50"),sQuery(id+"F16.wireOp",EDGE,"E51.0"),sQuery(id+"F16.wireOp",EDGE,"E52.0"),sQuery(id+"F16.wireOp",EDGE,"E53.0"),sQuery(id+"F16.wireOp",EDGE,"E54.0"),sQuery(id+"F16.wireOp",EDGE,"E55.0"),sQuery(id+"F16.wireOp",EDGE,"E56.0")])],"isStart":true})]}),makeQuery(id+"F23.opExtrude","CAP_FACE",FACE,{"disambiguationData":[OSD([sQuery(id+"F22.wireOp",EDGE,"E67"),sQuery(id+"F22.wireOp",EDGE,"E68"),sQuery(id+"F22.wireOp",EDGE,"E69"),sQuery(id+"F22.wireOp",EDGE,"E70")])],"isStart":true})]});
            var sketch = newSketch(context, id + "F24", { "sketchPlane" : qUnion([Q0])});
            skLineSegment(sketch, "E71", {"start": v(47.16, -9.24) * mm, "end": v(23.36, -50.46) * mm});
            skLineSegment(sketch, "E72", {"start": v(23.36, -50.46) * mm, "end": v(544.11, -50.46) * mm});
            skLineSegment(sketch, "E73", {"start": v(544.11, -50.46) * mm, "end": v(539.18, -9.24) * mm});
            skLineSegment(sketch, "E74", {"start": v(539.18, -9.24) * mm, "end": v(47.16, -9.24) * mm});
            skSolve(sketch);
        }
        {
            var Q0;
            Q0 = qSketchRegion(id + "F24", true);
            extrude(context, id + "F25", {"entities" : qUnion([Q0]), "operationType" : NewBodyOperationType.REMOVE, "oppositeDirection" : true, "depth" : 25 * mm});
        }
        {
            var Q0;
            Q0=makeQuery(id+"F23.boolean.opBoolean","MERGE",FACE,{"derivedFrom":[makeQuery(id+"F17.boolean.opBoolean","MERGE",FACE,{"derivedFrom":[makeQuery(id+"F14.boolean.opBoolean","MERGE",FACE,{"derivedFrom":[makeQuery(id+"F6.opExtrude","CAP_FACE",FACE,{"disambiguationData":[OSD([sQuery(id+"F5.wireOp",EDGE,"E11"),sQuery(id+"F5.wireOp",EDGE,"E12"),sQuery(id+"F5.wireOp",EDGE,"E13"),sQuery(id+"F5.wireOp",EDGE,"E14"),sQuery(id+"F5.wireOp",EDGE,"E15"),sQuery(id+"F5.wireOp",EDGE,"E16"),sQuery(id+"F5.wireOp",EDGE,"E17"),sQuery(id+"F5.wireOp",EDGE,"E19"),sQuery(id+"F5.wireOp",EDGE,"E22")])],"isStart":false}),makeQuery(id+"F14.opExtrude","CAP_FACE",FACE,{"disambiguationData":[OSD([sQuery(id+"F13.wireOp",EDGE,"E44"),sQuery(id+"F13.wireOp",EDGE,"E45"),sQuery(id+"F13.wireOp",EDGE,"E46"),sQuery(id+"F13.wireOp",EDGE,"E47")])],"isStart":false})]}),makeQuery(id+"F17.opExtrude","CAP_FACE",FACE,{"disambiguationData":[OSD([sQuery(id+"F16.wireOp",EDGE,"E48"),sQuery(id+"F16.wireOp",EDGE,"E49.0"),sQuery(id+"F16.wireOp",EDGE,"E49.1"),sQuery(id+"F16.wireOp",EDGE,"E49.2"),sQuery(id+"F16.wireOp",EDGE,"E49.3"),sQuery(id+"F16.wireOp",EDGE,"E49.4"),sQuery(id+"F16.wireOp",EDGE,"E49.5"),sQuery(id+"F16.wireOp",EDGE,"E50"),sQuery(id+"F16.wireOp",EDGE,"E51.0"),sQuery(id+"F16.wireOp",EDGE,"E52.0"),sQuery(id+"F16.wireOp",EDGE,"E53.0"),sQuery(id+"F16.wireOp",EDGE,"E54.0"),sQuery(id+"F16.wireOp",EDGE,"E55.0"),sQuery(id+"F16.wireOp",EDGE,"E56.0")])],"isStart":true})]}),makeQuery(id+"F23.opExtrude","CAP_FACE",FACE,{"disambiguationData":[OSD([sQuery(id+"F22.wireOp",EDGE,"E67"),sQuery(id+"F22.wireOp",EDGE,"E68"),sQuery(id+"F22.wireOp",EDGE,"E69"),sQuery(id+"F22.wireOp",EDGE,"E70")])],"isStart":true})]});
            var sketch = newSketch(context, id + "F26", { "sketchPlane" : qUnion([Q0])});
            skLineSegment(sketch, "E75", {"start": v(-23.36, -50.46) * mm, "end": v(0, -90.93) * mm});
            skLineSegment(sketch, "E76", {"start": v(0, -90.93) * mm, "end": v(23.36, -50.46) * mm});
            skLineSegment(sketch, "E77", {"start": v(23.36, -50.46) * mm, "end": v(-23.36, -50.46) * mm});
            skSolve(sketch);
        }
        {
            var Q0;
            Q0 = qSketchRegion(id + "F26", true);
            extrude(context, id + "F27", {"entities" : qUnion([Q0]), "operationType" : NewBodyOperationType.ADD, "oppositeDirection" : true, "depth" : 5 * mm});
        }
        {
            var Q0;
            {var subQ0=sQuery(id+"F5.wireOp",EDGE,"E17");var subQ1=makeQuery(id+"F6.opExtrude","SWEPT_FACE",FACE,{"disambiguationData":[OSD([subQ0])]});var subQ2=sQuery(id+"F5.wireOp",EDGE,"E19");var subQ3=makeQuery(id+"F6.opExtrude","SWEPT_FACE",FACE,{"disambiguationData":[OSD([subQ2])]});var subQ4=sQuery(id+"F5.wireOp",EDGE,"E22");var subQ5=sQuery(id+"F5.wireOp",EDGE,"E13");var subQ6=sQuery(id+"F5.wireOp",EDGE,"E12");var subQ7=makeQuery(id+"F6.opExtrude","SWEPT_FACE",FACE,{"disambiguationData":[OSD([subQ6,subQ5,subQ4])]});var subQ8=sQuery(id+"F2.wireOp",EDGE,"E10");var subQ9=sQuery(id+"F2.wireOp",EDGE,"E8");var subQ10=makeQuery(id+"F3.opSweep","CAP_FACE",FACE,{"disambiguationData":[OSD([sQuery(id+"F0.wireOp",VERTEX,"E4.end"),subQ9,sQuery(id+"F2.wireOp",EDGE,"E9"),subQ8])],"isStart":true});var subQ11=makeQuery(id+"F4.opPattern","COPY",FACE,{"derivedFrom":subQ10,"instanceName":"1"});var subQ12=sQuery(id+"F5.wireOp",EDGE,"E14");var subQ13=makeQuery(id+"F6.opExtrude","SWEPT_FACE",FACE,{"disambiguationData":[OSD([subQ12])]});var subQ14=sQuery(id+"F5.wireOp",EDGE,"E15");var subQ15=makeQuery(id+"F6.opExtrude","SWEPT_FACE",FACE,{"disambiguationData":[OSD([subQ14])]});var subQ16=sQuery(id+"F0.wireOp",EDGE,"E4");var subQ17=makeQuery(id+"F3.opSweep","SWEPT_FACE",FACE,{"disambiguationData":[OSD([subQ16,subQ8])]});var subQ18=makeQuery(id+"F4.opPattern","COPY",FACE,{"derivedFrom":subQ17,"instanceName":"1"});var subQ19=sQuery(id+"F5.wireOp",EDGE,"E16");var subQ20=makeQuery(id+"F6.opExtrude","SWEPT_FACE",FACE,{"disambiguationData":[OSD([subQ19])]});var subQ21=sQuery(id+"F0.wireOp",EDGE,"E5");var subQ22=makeQuery(id+"F3.opSweep","SWEPT_FACE",FACE,{"disambiguationData":[OSD([subQ21,subQ8])]});var subQ23=makeQuery(id+"F4.opPattern","COPY",FACE,{"derivedFrom":subQ22,"instanceName":"1"});var subQ24=makeQuery(id+"F3.opSweep","SWEPT_FACE",FACE,{"disambiguationData":[OSD([subQ16,subQ9])]});var subQ25=makeQuery(id+"F3.opSweep","SWEPT_FACE",FACE,{"disambiguationData":[OSD([sQuery(id+"F0.wireOp",EDGE,"E0"),subQ9])]});var subQ26=makeQuery(id+"F3.opSweep","SWEPT_FACE",FACE,{"disambiguationData":[OSD([subQ21,subQ9])]});var subQ27=makeQuery(id+"F4.opPattern","COPY",FACE,{"derivedFrom":subQ26,"instanceName":"1"});var subQ28=makeQuery(id+"F3.opSweep","SWEPT_FACE",FACE,{"disambiguationData":[OSD([sQuery(id+"F0.wireOp",EDGE,"E7"),subQ9])]});var subQ29=makeQuery(id+"F4.opPattern","COPY",FACE,{"derivedFrom":subQ24,"instanceName":"1"});var subQ30=makeQuery(id+"F4.opPattern","COPY",FACE,{"derivedFrom":subQ25,"instanceName":"1"});var subQ31=makeQuery(id+"F4.opPattern","COPY",FACE,{"derivedFrom":subQ28,"instanceName":"1"});var subQ32=sQuery(id+"F5.wireOp",EDGE,"E11");var subQ33=makeQuery(id+"F6.opExtrude","SWEPT_FACE",FACE,{"disambiguationData":[OSD([subQ32])]});Q0=makeQuery(id+"F27.boolean.opBoolean","MERGE",FACE,{"derivedFrom":[makeQuery(id+"F23.boolean.opBoolean","MERGE",FACE,{"derivedFrom":[makeQuery(id+"F17.boolean.opBoolean","MERGE",FACE,{"derivedFrom":[makeQuery(id+"F14.boolean.opBoolean","MERGE",FACE,{"derivedFrom":[makeQuery(id+"F8.boolean.opBoolean","SPLIT",FACE,{"disambiguationData":[TD([subQ33])],"derivedFrom":makeQuery(id+"F6.boolean.opBoolean","SPLIT",FACE,{"disambiguationData":[TD([subQ10,subQ25,subQ24,subQ17,subQ26,subQ22,subQ28,subQ11,subQ30,subQ29,subQ18,subQ27,subQ23,subQ31,subQ33,subQ7,subQ13,subQ15,subQ20,subQ1,subQ3])],"derivedFrom":makeQuery(id+"F6.opExtrude","CAP_FACE",FACE,{"disambiguationData":[OSD([subQ32,subQ6,subQ5,subQ12,subQ14,subQ19,subQ0,subQ2,subQ4])],"isStart":true})})}),makeQuery(id+"F14.opExtrude","CAP_FACE",FACE,{"disambiguationData":[OSD([sQuery(id+"F13.wireOp",EDGE,"E44"),sQuery(id+"F13.wireOp",EDGE,"E45"),sQuery(id+"F13.wireOp",EDGE,"E46"),sQuery(id+"F13.wireOp",EDGE,"E47")])],"isStart":true})]}),makeQuery(id+"F17.opExtrude","CAP_FACE",FACE,{"disambiguationData":[OSD([sQuery(id+"F16.wireOp",EDGE,"E48"),sQuery(id+"F16.wireOp",EDGE,"E49.0"),sQuery(id+"F16.wireOp",EDGE,"E49.1"),sQuery(id+"F16.wireOp",EDGE,"E49.2"),sQuery(id+"F16.wireOp",EDGE,"E49.3"),sQuery(id+"F16.wireOp",EDGE,"E49.4"),sQuery(id+"F16.wireOp",EDGE,"E49.5"),sQuery(id+"F16.wireOp",EDGE,"E50"),sQuery(id+"F16.wireOp",EDGE,"E51.0"),sQuery(id+"F16.wireOp",EDGE,"E52.0"),sQuery(id+"F16.wireOp",EDGE,"E53.0"),sQuery(id+"F16.wireOp",EDGE,"E54.0"),sQuery(id+"F16.wireOp",EDGE,"E55.0"),sQuery(id+"F16.wireOp",EDGE,"E56.0")])],"isStart":false})]}),makeQuery(id+"F23.opExtrude","CAP_FACE",FACE,{"disambiguationData":[OSD([sQuery(id+"F22.wireOp",EDGE,"E67"),sQuery(id+"F22.wireOp",EDGE,"E68"),sQuery(id+"F22.wireOp",EDGE,"E69"),sQuery(id+"F22.wireOp",EDGE,"E70")])],"isStart":false})]}),makeQuery(id+"F27.opExtrude","CAP_FACE",FACE,{"disambiguationData":[OSD([sQuery(id+"F26.wireOp",EDGE,"E75"),sQuery(id+"F26.wireOp",EDGE,"E76"),sQuery(id+"F26.wireOp",EDGE,"E77")])],"isStart":false})]});}
            var sketch = newSketch(context, id + "F28", { "sketchPlane" : qUnion([Q0])});
            skLineSegment(sketch, "E78.0", {"start": v(0, 76.93) * mm, "end": v(22.78, 37.46) * mm});
            skLineSegment(sketch, "E78.1", {"start": v(-22.78, 37.46) * mm, "end": v(0, 76.93) * mm});
            skLineSegment(sketch, "E79", {"start": v(-22.78, 37.46) * mm, "end": v(22.78, 37.46) * mm});
            skSolve(sketch);
        }
        {
            var Q0;
            Q0 = qSketchRegion(id + "F28", true);
            extrude(context, id + "F29", {"entities" : qUnion([Q0]), "operationType" : NewBodyOperationType.REMOVE, "oppositeDirection" : true, "depth" : 25 * mm});
        }
        {
            var Q0;
            {var subQ0=sQuery(id+"F5.wireOp",EDGE,"E17");var subQ1=makeQuery(id+"F6.opExtrude","SWEPT_FACE",FACE,{"disambiguationData":[OSD([subQ0])]});var subQ2=sQuery(id+"F5.wireOp",EDGE,"E19");var subQ3=makeQuery(id+"F6.opExtrude","SWEPT_FACE",FACE,{"disambiguationData":[OSD([subQ2])]});var subQ4=sQuery(id+"F5.wireOp",EDGE,"E22");var subQ5=sQuery(id+"F5.wireOp",EDGE,"E13");var subQ6=sQuery(id+"F5.wireOp",EDGE,"E12");var subQ7=makeQuery(id+"F6.opExtrude","SWEPT_FACE",FACE,{"disambiguationData":[OSD([subQ6,subQ5,subQ4])]});var subQ8=sQuery(id+"F2.wireOp",EDGE,"E10");var subQ9=sQuery(id+"F2.wireOp",EDGE,"E8");var subQ10=makeQuery(id+"F3.opSweep","CAP_FACE",FACE,{"disambiguationData":[OSD([sQuery(id+"F0.wireOp",VERTEX,"E4.end"),subQ9,sQuery(id+"F2.wireOp",EDGE,"E9"),subQ8])],"isStart":true});var subQ11=makeQuery(id+"F4.opPattern","COPY",FACE,{"derivedFrom":subQ10,"instanceName":"1"});var subQ12=sQuery(id+"F5.wireOp",EDGE,"E14");var subQ13=makeQuery(id+"F6.opExtrude","SWEPT_FACE",FACE,{"disambiguationData":[OSD([subQ12])]});var subQ14=sQuery(id+"F5.wireOp",EDGE,"E15");var subQ15=makeQuery(id+"F6.opExtrude","SWEPT_FACE",FACE,{"disambiguationData":[OSD([subQ14])]});var subQ16=sQuery(id+"F0.wireOp",EDGE,"E4");var subQ17=makeQuery(id+"F3.opSweep","SWEPT_FACE",FACE,{"disambiguationData":[OSD([subQ16,subQ8])]});var subQ18=makeQuery(id+"F4.opPattern","COPY",FACE,{"derivedFrom":subQ17,"instanceName":"1"});var subQ19=sQuery(id+"F5.wireOp",EDGE,"E16");var subQ20=makeQuery(id+"F6.opExtrude","SWEPT_FACE",FACE,{"disambiguationData":[OSD([subQ19])]});var subQ21=sQuery(id+"F0.wireOp",EDGE,"E5");var subQ22=makeQuery(id+"F3.opSweep","SWEPT_FACE",FACE,{"disambiguationData":[OSD([subQ21,subQ8])]});var subQ23=makeQuery(id+"F4.opPattern","COPY",FACE,{"derivedFrom":subQ22,"instanceName":"1"});var subQ24=makeQuery(id+"F3.opSweep","SWEPT_FACE",FACE,{"disambiguationData":[OSD([subQ16,subQ9])]});var subQ25=makeQuery(id+"F3.opSweep","SWEPT_FACE",FACE,{"disambiguationData":[OSD([sQuery(id+"F0.wireOp",EDGE,"E0"),subQ9])]});var subQ26=makeQuery(id+"F3.opSweep","SWEPT_FACE",FACE,{"disambiguationData":[OSD([subQ21,subQ9])]});var subQ27=makeQuery(id+"F4.opPattern","COPY",FACE,{"derivedFrom":subQ26,"instanceName":"1"});var subQ28=makeQuery(id+"F3.opSweep","SWEPT_FACE",FACE,{"disambiguationData":[OSD([sQuery(id+"F0.wireOp",EDGE,"E7"),subQ9])]});var subQ29=makeQuery(id+"F4.opPattern","COPY",FACE,{"derivedFrom":subQ24,"instanceName":"1"});var subQ30=makeQuery(id+"F4.opPattern","COPY",FACE,{"derivedFrom":subQ25,"instanceName":"1"});var subQ31=makeQuery(id+"F4.opPattern","COPY",FACE,{"derivedFrom":subQ28,"instanceName":"1"});var subQ32=sQuery(id+"F5.wireOp",EDGE,"E11");var subQ33=makeQuery(id+"F6.opExtrude","SWEPT_FACE",FACE,{"disambiguationData":[OSD([subQ32])]});Q0=makeQuery(id+"F27.boolean.opBoolean","MERGE",FACE,{"derivedFrom":[makeQuery(id+"F23.boolean.opBoolean","MERGE",FACE,{"derivedFrom":[makeQuery(id+"F17.boolean.opBoolean","MERGE",FACE,{"derivedFrom":[makeQuery(id+"F14.boolean.opBoolean","MERGE",FACE,{"derivedFrom":[makeQuery(id+"F8.boolean.opBoolean","SPLIT",FACE,{"disambiguationData":[TD([subQ33])],"derivedFrom":makeQuery(id+"F6.boolean.opBoolean","SPLIT",FACE,{"disambiguationData":[TD([subQ10,subQ25,subQ24,subQ17,subQ26,subQ22,subQ28,subQ11,subQ30,subQ29,subQ18,subQ27,subQ23,subQ31,subQ33,subQ7,subQ13,subQ15,subQ20,subQ1,subQ3])],"derivedFrom":makeQuery(id+"F6.opExtrude","CAP_FACE",FACE,{"disambiguationData":[OSD([subQ32,subQ6,subQ5,subQ12,subQ14,subQ19,subQ0,subQ2,subQ4])],"isStart":true})})}),makeQuery(id+"F14.opExtrude","CAP_FACE",FACE,{"disambiguationData":[OSD([sQuery(id+"F13.wireOp",EDGE,"E44"),sQuery(id+"F13.wireOp",EDGE,"E45"),sQuery(id+"F13.wireOp",EDGE,"E46"),sQuery(id+"F13.wireOp",EDGE,"E47")])],"isStart":true})]}),makeQuery(id+"F17.opExtrude","CAP_FACE",FACE,{"disambiguationData":[OSD([sQuery(id+"F16.wireOp",EDGE,"E48"),sQuery(id+"F16.wireOp",EDGE,"E49.0"),sQuery(id+"F16.wireOp",EDGE,"E49.1"),sQuery(id+"F16.wireOp",EDGE,"E49.2"),sQuery(id+"F16.wireOp",EDGE,"E49.3"),sQuery(id+"F16.wireOp",EDGE,"E49.4"),sQuery(id+"F16.wireOp",EDGE,"E49.5"),sQuery(id+"F16.wireOp",EDGE,"E50"),sQuery(id+"F16.wireOp",EDGE,"E51.0"),sQuery(id+"F16.wireOp",EDGE,"E52.0"),sQuery(id+"F16.wireOp",EDGE,"E53.0"),sQuery(id+"F16.wireOp",EDGE,"E54.0"),sQuery(id+"F16.wireOp",EDGE,"E55.0"),sQuery(id+"F16.wireOp",EDGE,"E56.0")])],"isStart":false})]}),makeQuery(id+"F23.opExtrude","CAP_FACE",FACE,{"disambiguationData":[OSD([sQuery(id+"F22.wireOp",EDGE,"E67"),sQuery(id+"F22.wireOp",EDGE,"E68"),sQuery(id+"F22.wireOp",EDGE,"E69"),sQuery(id+"F22.wireOp",EDGE,"E70")])],"isStart":false})]}),makeQuery(id+"F27.opExtrude","CAP_FACE",FACE,{"disambiguationData":[OSD([sQuery(id+"F26.wireOp",EDGE,"E75"),sQuery(id+"F26.wireOp",EDGE,"E76"),sQuery(id+"F26.wireOp",EDGE,"E77")])],"isStart":false})]});}
            var sketch = newSketch(context, id + "F30", { "sketchPlane" : qUnion([Q0])});
            skLineSegment(sketch, "E80", {"start": v(511.17, 9.24) * mm, "end": v(554.66, -34.25) * mm});
            skLineSegment(sketch, "E81", {"start": v(554.66, -34.25) * mm, "end": v(554.66, -68.8) * mm});
            skLineSegment(sketch, "E82", {"start": v(554.66, -68.8) * mm, "end": v(625.48, -104.92) * mm});
            skLineSegment(sketch, "E83", {"start": v(625.48, -104.92) * mm, "end": v(600.4, 15.8) * mm});
            skLineSegment(sketch, "E84", {"start": v(600.4, 15.8) * mm, "end": v(526.22, 40.34) * mm});
            skLineSegment(sketch, "E85", {"start": v(526.22, 40.34) * mm, "end": v(511.17, 9.24) * mm});
            skSolve(sketch);
        }
        {
            var Q0;
            Q0 = qSketchRegion(id + "F30", true);
            extrude(context, id + "F31", {"entities" : qUnion([Q0]), "operationType" : NewBodyOperationType.REMOVE, "oppositeDirection" : true, "depth" : 25 * mm});
        }
        {
            var Q0;
            Q0=makeQuery(id+"F27.boolean.opBoolean","MERGE",FACE,{"derivedFrom":[makeQuery(id+"F23.boolean.opBoolean","MERGE",FACE,{"derivedFrom":[makeQuery(id+"F17.boolean.opBoolean","MERGE",FACE,{"derivedFrom":[makeQuery(id+"F14.boolean.opBoolean","MERGE",FACE,{"derivedFrom":[makeQuery(id+"F6.opExtrude","CAP_FACE",FACE,{"disambiguationData":[OSD([sQuery(id+"F5.wireOp",EDGE,"E11"),sQuery(id+"F5.wireOp",EDGE,"E12"),sQuery(id+"F5.wireOp",EDGE,"E13"),sQuery(id+"F5.wireOp",EDGE,"E14"),sQuery(id+"F5.wireOp",EDGE,"E15"),sQuery(id+"F5.wireOp",EDGE,"E16"),sQuery(id+"F5.wireOp",EDGE,"E17"),sQuery(id+"F5.wireOp",EDGE,"E19"),sQuery(id+"F5.wireOp",EDGE,"E22")])],"isStart":false}),makeQuery(id+"F14.opExtrude","CAP_FACE",FACE,{"disambiguationData":[OSD([sQuery(id+"F13.wireOp",EDGE,"E44"),sQuery(id+"F13.wireOp",EDGE,"E45"),sQuery(id+"F13.wireOp",EDGE,"E46"),sQuery(id+"F13.wireOp",EDGE,"E47")])],"isStart":false})]}),makeQuery(id+"F17.opExtrude","CAP_FACE",FACE,{"disambiguationData":[OSD([sQuery(id+"F16.wireOp",EDGE,"E48"),sQuery(id+"F16.wireOp",EDGE,"E49.0"),sQuery(id+"F16.wireOp",EDGE,"E49.1"),sQuery(id+"F16.wireOp",EDGE,"E49.2"),sQuery(id+"F16.wireOp",EDGE,"E49.3"),sQuery(id+"F16.wireOp",EDGE,"E49.4"),sQuery(id+"F16.wireOp",EDGE,"E49.5"),sQuery(id+"F16.wireOp",EDGE,"E50"),sQuery(id+"F16.wireOp",EDGE,"E51.0"),sQuery(id+"F16.wireOp",EDGE,"E52.0"),sQuery(id+"F16.wireOp",EDGE,"E53.0"),sQuery(id+"F16.wireOp",EDGE,"E54.0"),sQuery(id+"F16.wireOp",EDGE,"E55.0"),sQuery(id+"F16.wireOp",EDGE,"E56.0")])],"isStart":true})]}),makeQuery(id+"F23.opExtrude","CAP_FACE",FACE,{"disambiguationData":[OSD([sQuery(id+"F22.wireOp",EDGE,"E67"),sQuery(id+"F22.wireOp",EDGE,"E68"),sQuery(id+"F22.wireOp",EDGE,"E69"),sQuery(id+"F22.wireOp",EDGE,"E70")])],"isStart":true})]}),makeQuery(id+"F27.opExtrude","CAP_FACE",FACE,{"disambiguationData":[OSD([sQuery(id+"F26.wireOp",EDGE,"E75"),sQuery(id+"F26.wireOp",EDGE,"E76"),sQuery(id+"F26.wireOp",EDGE,"E77")])],"isStart":true})]});
            extrude(context, id + "F32", {"entities" : qUnion([Q0]), "operationType" : NewBodyOperationType.ADD, "depth" : 4 * mm});
        }
    });
